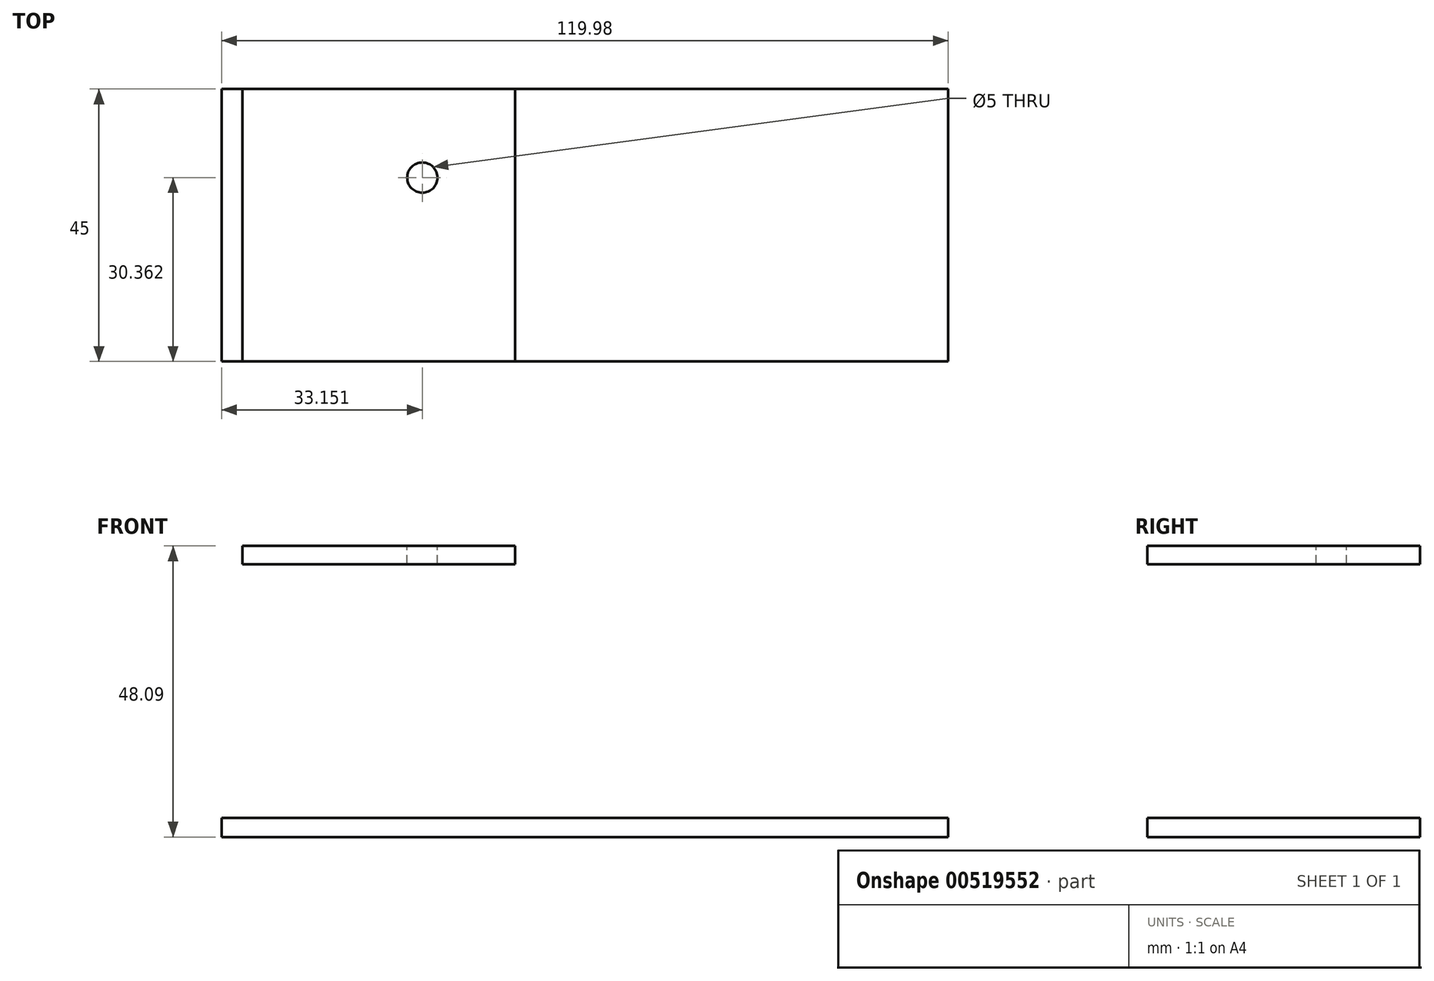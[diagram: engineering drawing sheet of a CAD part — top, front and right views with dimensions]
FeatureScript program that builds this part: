
annotation { "Feature Type Name" : "Feature", "Feature Type Description" : "" }
export const myFeature = defineFeature(function(context is Context, id is Id, definition is map)
    precondition{}
    {
        {
            var Q0;
            Q0=qCreatedBy(makeId("Front.planeOp"),FACE);
            var sketch = newSketch(context, id + "F0", { "sketchPlane" : qUnion([Q0])});
            skLineSegment(sketch, "E0.bottom", {"start": v(68.66, -23.57) * mm, "end": v(-51.32, -23.57) * mm});
            skLineSegment(sketch, "E0.top", {"start": v(68.66, -20.42) * mm, "end": v(-51.32, -20.42) * mm});
            skLineSegment(sketch, "E0.left", {"start": v(68.66, -23.57) * mm, "end": v(68.66, -20.42) * mm});
            skLineSegment(sketch, "E0.right", {"start": v(-51.32, -23.57) * mm, "end": v(-51.32, -20.42) * mm});
            skLineSegment(sketch, "E1.bottom", {"start": v(-51.32, -20.42) * mm, "end": v(-47.85, -20.42) * mm});
            skLineSegment(sketch, "E1.top", {"start": v(-51.32, 24.52) * mm, "end": v(-47.85, 24.52) * mm});
            skLineSegment(sketch, "E1.left", {"start": v(-51.32, -20.42) * mm, "end": v(-51.32, 24.52) * mm});
            skLineSegment(sketch, "E1.right", {"start": v(-47.85, -20.42) * mm, "end": v(-47.85, 24.52) * mm});
            skLineSegment(sketch, "E2.bottom", {"start": v(-47.85, 24.52) * mm, "end": v(-2.85, 24.52) * mm});
            skLineSegment(sketch, "E2.top", {"start": v(-47.85, 21.52) * mm, "end": v(-2.85, 21.52) * mm});
            skLineSegment(sketch, "E2.left", {"start": v(-47.85, 24.52) * mm, "end": v(-47.85, 21.52) * mm});
            skLineSegment(sketch, "E2.right", {"start": v(-2.85, 24.52) * mm, "end": v(-2.85, 21.52) * mm});
            skSolve(sketch);
        }
        {
            var Q0;
            Q0=makeQuery(id+"F0.imprint","IMPRINT",FACE,{"disambiguationData":[TD([[makeQuery(id+"F0.imprint","IMPRINT",EDGE,{"derivedFrom":sQuery(id+"F0.wireOp",EDGE,"E2.bottom")}),-1.0]])]});
            var Q1;
            Q1=makeQuery(id+"F0.imprint","IMPRINT",FACE,{"disambiguationData":[TD([[makeQuery(id+"F0.imprint","IMPRINT",EDGE,{"derivedFrom":sQuery(id+"F0.wireOp",EDGE,"E0.bottom")}),-1.0]])]});
            var Q2;
            Q2=makeQuery(id+"F0.imprint","IMPRINT",FACE,{"disambiguationData":[TD([[makeQuery(id+"F0.imprint","IMPRINT",EDGE,{"derivedFrom":sQuery(id+"F0.wireOp",EDGE,"E1.bottom")}),1.0]])]});
            extrude(context, id + "F1", {"entities" : qUnion([Q0, Q1, Q2]), "depth" : 45 * mm, "offsetDistance" : 25 * mm});
        }
        {
            var Q0;
            Q0=makeQuery(id+"F1.opExtrude","SWEPT_FACE",FACE,{"disambiguationData":[OSD([sQuery(id+"F0.wireOp",EDGE,"E1.top"),sQuery(id+"F0.wireOp",EDGE,"E2.bottom")])]});
            var sketch = newSketch(context, id + "F2", { "sketchPlane" : qUnion([Q0])});
            skCircle(sketch, "E3", {"center": v(-18.17, -14.64) * mm, "radius": 2.36 * mm});
            skSolve(sketch);
        }
        {
            var Q0;
            Q0=sQuery(id+"F2.wireOp",VERTEX,"E3.center");
            var Q1;
            Q1=makeQuery(id+"F1.opExtrude","SWEPT_BODY",BODY,{"disambiguationData":[OSD([sQuery(id+"F0.wireOp",EDGE,"E0.bottom"),sQuery(id+"F0.wireOp",EDGE,"E0.top"),sQuery(id+"F0.wireOp",EDGE,"E0.left"),sQuery(id+"F0.wireOp",EDGE,"E0.right"),sQuery(id+"F0.wireOp",EDGE,"E1.top"),sQuery(id+"F0.wireOp",EDGE,"E1.left"),sQuery(id+"F0.wireOp",EDGE,"E1.right"),sQuery(id+"F0.wireOp",EDGE,"E2.bottom"),sQuery(id+"F0.wireOp",EDGE,"E2.top"),sQuery(id+"F0.wireOp",EDGE,"E2.right")])]});
            hole(context, id + "F3", {"style" : HoleStyle.SIMPLE, "endStyle" : HoleEndStyle.BLIND, "holeDiameter" : 5 * mm, "holeDepth" : 12 * mm, "isTappedThrough" : true, "tappedDepth" : 12 * mm, "tapClearance" : 3, "locations" : qUnion([Q0]), "scope" : qUnion([Q1])});
        }
    });
